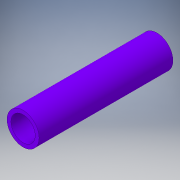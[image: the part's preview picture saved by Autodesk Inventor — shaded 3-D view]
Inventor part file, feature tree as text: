
AUTODESK INVENTOR PART (.ipt)
format: ipt  version: 2018 (Build 220112000, 112)  size: 108,032 bytes
history: native  units: in
note: dims shown in document units (in); Inventor stores cm internally (conversion verified against a paired STEP export)
features: extrude x1, sketch x1
ambient origin geometry x8: Origin, YZ Plane, XZ Plane, XY Plane, X Axis, Y Axis, Z Axis, Center Point
bodies: Solid1 (feature_tree)
feature tree (2):
  extrude  "Extrusion1"  Depth=5.5in
  sketch  "Sketch1"  dims[d0=1.315in d1=1.0in d2=5.5in d3=0.0in]
